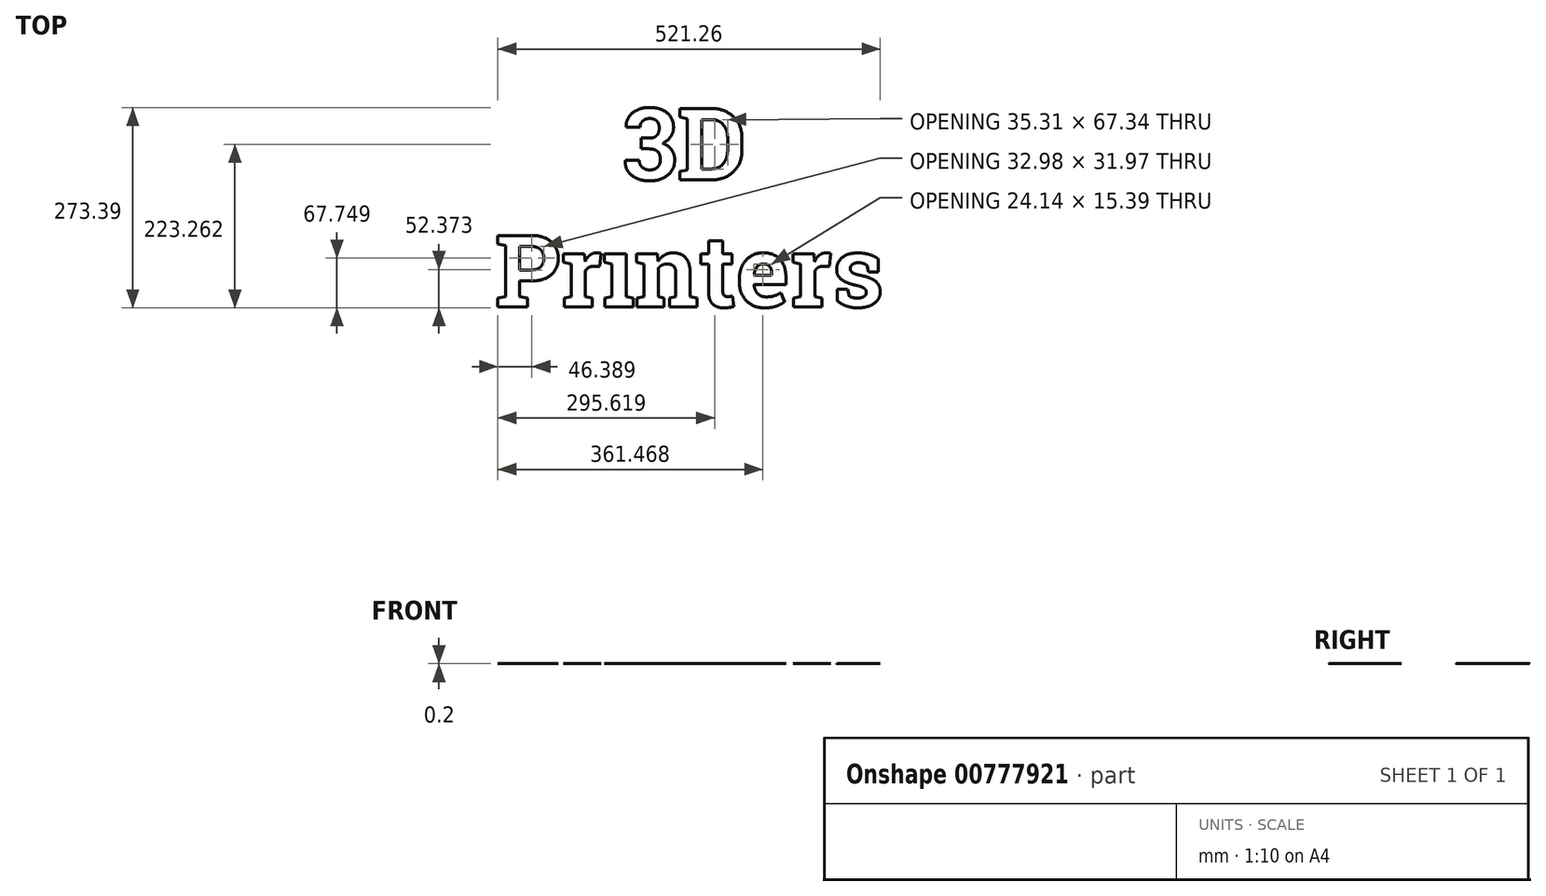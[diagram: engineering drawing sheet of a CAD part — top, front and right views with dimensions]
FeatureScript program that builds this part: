
annotation { "Feature Type Name" : "Feature", "Feature Type Description" : "" }
export const myFeature = defineFeature(function(context is Context, id is Id, definition is map)
    precondition{}
    {
        {
            var Q0;
            Q0=qCreatedBy(makeId("Top.planeOp"),FACE);
            var sketch = newSketch(context, id + "F0", { "sketchPlane" : qUnion([Q0])});
            skText(sketch, "E0", { "text": "Printers", "fontName": "RobotoSlab-Bold.ttf"});
            skText(sketch, "E1", { "text": "3D", "fontName": "RobotoSlab-Bold.ttf"});
            const initialGuessF0  = {"E0": [-0.11773, -0.05516, 1, 0, 0.09861], "E1": [0.05597, 0.11804, 1, 0, 0.09861]};
            skSetInitialGuess(sketch, initialGuessF0);
            skSolve(sketch);
        }
        {
            var Q0;
            Q0=makeQuery(id+"F0.imprint","IMPRINT",FACE,{"disambiguationData":[TD([[makeQuery(id+"F0.imprint","IMPRINT",EDGE,{"derivedFrom":sQuery(id+"F0.wireOp",EDGE,"E1.sketch_text.stroke-0")}),-1.0]])]});
            var Q1;
            Q1=makeQuery(id+"F0.imprint","IMPRINT",FACE,{"disambiguationData":[TD([[makeQuery(id+"F0.imprint","IMPRINT",EDGE,{"derivedFrom":sQuery(id+"F0.wireOp",EDGE,"E1.sketch_text.stroke-31")}),-1.0]])]});
            var Q2;
            Q2=makeQuery(id+"F0.imprint","IMPRINT",FACE,{"disambiguationData":[TD([[makeQuery(id+"F0.imprint","IMPRINT",EDGE,{"derivedFrom":sQuery(id+"F0.wireOp",EDGE,"E0.sketch_text.stroke-0")}),-1.0]])]});
            var Q3;
            Q3=makeQuery(id+"F0.imprint","IMPRINT",FACE,{"disambiguationData":[TD([[makeQuery(id+"F0.imprint","IMPRINT",EDGE,{"derivedFrom":sQuery(id+"F0.wireOp",EDGE,"E0.sketch_text.stroke-23")}),-1.0]])]});
            var Q4;
            Q4=makeQuery(id+"F0.imprint","IMPRINT",FACE,{"disambiguationData":[TD([[makeQuery(id+"F0.imprint","IMPRINT",EDGE,{"derivedFrom":sQuery(id+"F0.wireOp",EDGE,"E0.sketch_text.stroke-42")}),-1.0]])]});
            var Q5;
            Q5=makeQuery(id+"F0.imprint","IMPRINT",FACE,{"disambiguationData":[TD([[makeQuery(id+"F0.imprint","IMPRINT",EDGE,{"derivedFrom":sQuery(id+"F0.wireOp",EDGE,"E0.sketch_text.stroke-56")}),-1.0]])]});
            var Q6;
            Q6=makeQuery(id+"F0.imprint","IMPRINT",FACE,{"disambiguationData":[TD([[makeQuery(id+"F0.imprint","IMPRINT",EDGE,{"derivedFrom":sQuery(id+"F0.wireOp",EDGE,"E0.sketch_text.stroke-82")}),-1.0]])]});
            var Q7;
            Q7=makeQuery(id+"F0.imprint","IMPRINT",FACE,{"disambiguationData":[TD([[makeQuery(id+"F0.imprint","IMPRINT",EDGE,{"derivedFrom":sQuery(id+"F0.wireOp",EDGE,"E0.sketch_text.stroke-102")}),-1.0]])]});
            var Q8;
            Q8=makeQuery(id+"F0.imprint","IMPRINT",FACE,{"disambiguationData":[TD([[makeQuery(id+"F0.imprint","IMPRINT",EDGE,{"derivedFrom":sQuery(id+"F0.wireOp",EDGE,"E0.sketch_text.stroke-126")}),-1.0]])]});
            var Q9;
            Q9=makeQuery(id+"F0.imprint","IMPRINT",FACE,{"disambiguationData":[TD([[makeQuery(id+"F0.imprint","IMPRINT",EDGE,{"derivedFrom":sQuery(id+"F0.wireOp",EDGE,"E0.sketch_text.stroke-145")}),-1.0]])]});
            extrude(context, id + "F1", {"entities" : qUnion([Q0, Q1, Q2, Q3, Q4, Q5, Q6, Q7, Q8, Q9]), "depth" : .2 * mm, "offsetDistance" : 25.4 * mm});
        }
    });
